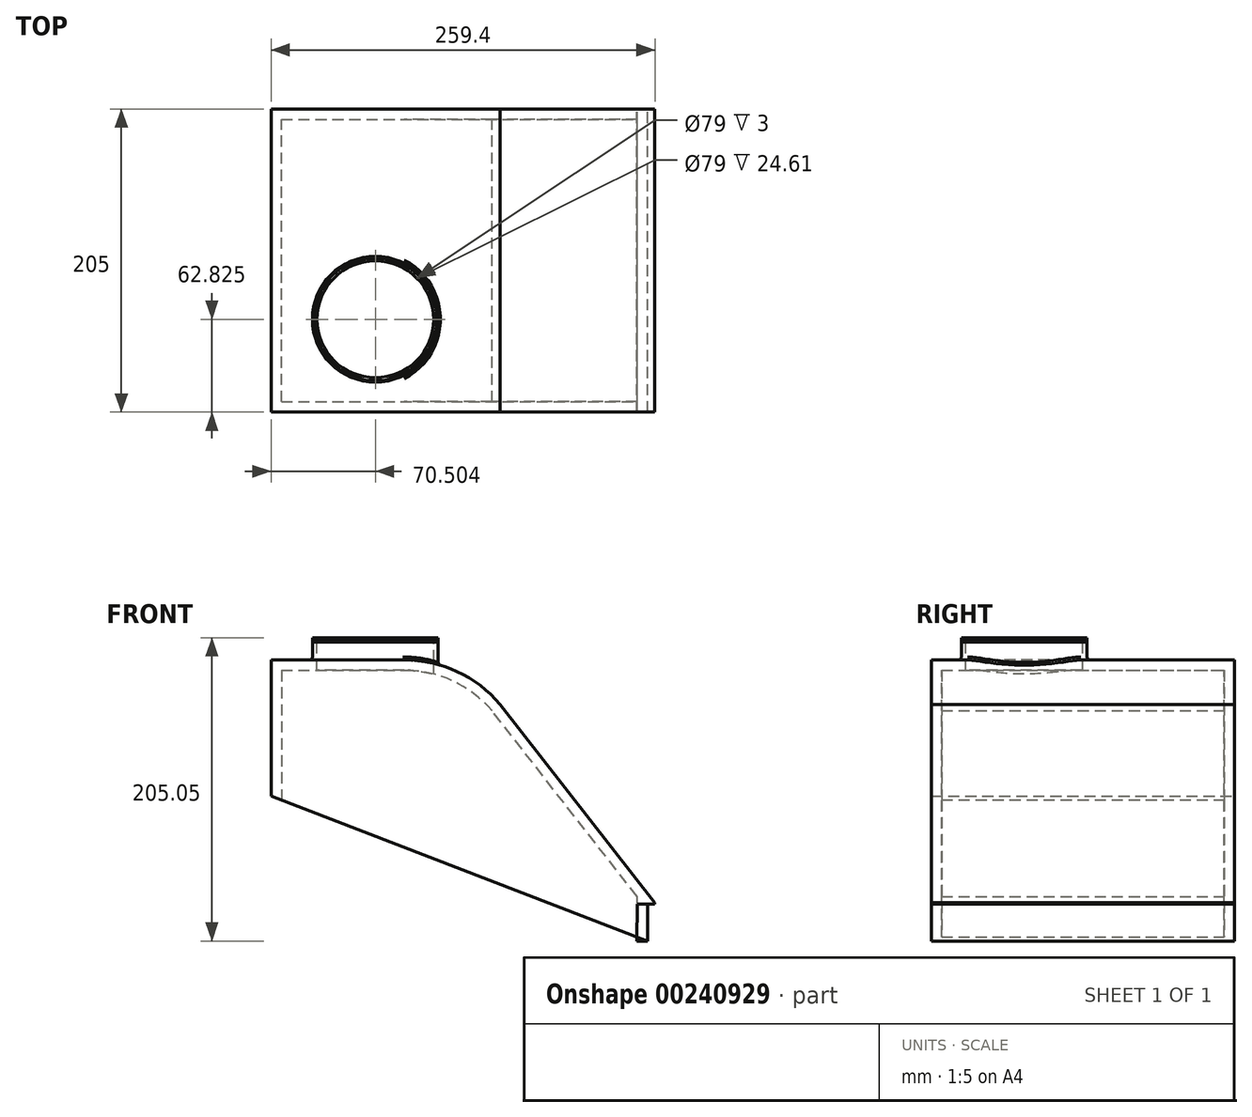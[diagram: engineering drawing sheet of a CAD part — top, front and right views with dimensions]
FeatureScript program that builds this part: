
annotation { "Feature Type Name" : "Feature", "Feature Type Description" : "" }
export const myFeature = defineFeature(function(context is Context, id is Id, definition is map)
    precondition{}
    {
        {
            var Q0;
            Q0=qCreatedBy(makeId("Front.planeOp"),FACE);
            var sketch = newSketch(context, id + "F0", { "sketchPlane" : qUnion([Q0])});
            skLineSegment(sketch, "E0", {"start": v(-34.53, -28) * mm, "end": v(265.47, -28) * mm, "construction": true});
            skLineSegment(sketch, "E1", {"start": v(-17.19, 164) * mm, "end": v(72.81, 164) * mm});
            skLineSegment(sketch, "E2", {"start": v(-17.19, 164) * mm, "end": v(-17.19, 72) * mm});
            skLineSegment(sketch, "E3", {"start": v(-17.19, 72) * mm, "end": v(242.2, -28) * mm});
            skLineSegment(sketch, "E4", {"start": v(242.2, 0) * mm, "end": v(137.6, 134) * mm});
            skLineSegment(sketch, "E5", {"start": v(-17.19, 72) * mm, "end": v(-17.19, -28) * mm, "construction": true});
            skLineSegment(sketch, "E6", {"start": v(242.2, 0) * mm, "end": v(137.2, 0) * mm, "construction": true});
            skArc(sketch, "E7", {"start": v(137.6, 134) * mm, "mid": v(108.5, 156.14) * mm, "end": v(72.81, 164) * mm});
            skLineSegment(sketch, "E8.top", {"start": v(242.2, -1) * mm, "end": v(237.2, -1) * mm});
            skLineSegment(sketch, "E9", {"start": v(242.2, 0) * mm, "end": v(242.2, -1) * mm});
            skLineSegment(sketch, "E10", {"start": v(237.14, -26.05) * mm, "end": v(237.2, -1) * mm});
            skPoint(sketch, "E11", {"position": v(237.14, -26.05) * mm});
            skPoint(sketch, "E12", {"position": v(242.2, -28) * mm});
            skSolve(sketch);
        }
        {
            var Q0;
            Q0=makeQuery(id+"F0.imprint","IMPRINT",FACE,{"disambiguationData":[TD([[makeQuery(id+"F0.imprint","IMPRINT",EDGE,{"derivedFrom":sQuery(id+"F0.wireOp",EDGE,"E1")}),-1.0]])]});
            extrude(context, id + "F1", {"entities" : qUnion([Q0]), "depth" : 100 * mm});
        }
        {
            var Q0;
            Q0=makeQuery(id+"F1.opExtrude","CAP_FACE",FACE,{"disambiguationData":[OSD([sQuery(id+"F0.wireOp",EDGE,"E1"),sQuery(id+"F0.wireOp",EDGE,"E2"),sQuery(id+"F0.wireOp",EDGE,"E3"),sQuery(id+"F0.wireOp",EDGE,"E4"),sQuery(id+"F0.wireOp",EDGE,"E7"),sQuery(id+"F0.wireOp",EDGE,"E8.top"),sQuery(id+"F0.wireOp",EDGE,"E9"),sQuery(id+"F0.wireOp",EDGE,"E10")])],"isStart":false});
            extrude(context, id + "F2", {"entities" : qUnion([Q0]), "operationType" : NewBodyOperationType.ADD, "depth" : 105 * mm});
        }
        {
            var Q0;
            {var subQ0=sQuery(id+"F0.wireOp",EDGE,"E3");Q0=makeQuery(id+"F2.boolean.opBoolean","MERGE",FACE,{"derivedFrom":[makeQuery(id+"F1.opExtrude","SWEPT_FACE",FACE,{"disambiguationData":[OSD([subQ0])]}),makeQuery(id+"F2.opExtrude","SWEPT_FACE",FACE,{"disambiguationData":[OSD([subQ0])]})]});}
            shell(context, id + "F3", {"entities" : qUnion([Q0]), "thickness" : 7 * mm});
        }
        {
            var Q0;
            {var subQ0=sQuery(id+"F0.wireOp",EDGE,"E1");Q0=makeQuery(id+"F2.boolean.opBoolean","MERGE",FACE,{"derivedFrom":[makeQuery(id+"F1.opExtrude","SWEPT_FACE",FACE,{"disambiguationData":[OSD([subQ0])]}),makeQuery(id+"F2.opExtrude","SWEPT_FACE",FACE,{"disambiguationData":[OSD([subQ0])]})]});}
            cPlane(context, id + "F4", {"entities" : qUnion([Q0]), "cplaneType" : CPlaneType.OFFSET, "offset" : 15 * mm, "width" : 150 * mm, "height" : 150 * mm});
        }
        {
            var Q0;
            Q0=qCreatedBy(id+"F4.planeOp",FACE);
            var sketch = newSketch(context, id + "F5", { "sketchPlane" : qUnion([Q0])});
            skCircle(sketch, "E13", {"center": v(53.31, -142.18) * mm, "radius": 42.5 * mm});
            skLineSegment(sketch, "E14", {"start": v(10.81, 14.75) * mm, "end": v(10.81, -239.37) * mm, "construction": true});
            skLineSegment(sketch, "E15", {"start": v(-63, -185) * mm, "end": v(117.93, -185) * mm, "construction": true});
            skSolve(sketch);
        }
        {
            var Q0;
            Q0=makeQuery(id+"F5.imprint","IMPRINT",FACE,{"disambiguationData":[TD([[makeQuery(id+"F5.imprint","IMPRINT",EDGE,{"derivedFrom":sQuery(id+"F5.wireOp",EDGE,"E13")}),1.0]])]});
            extrude(context, id + "F6", {"entities" : qUnion([Q0]), "operationType" : NewBodyOperationType.ADD, "oppositeDirection" : true, "depth" : 20 * mm});
        }
        {
            var Q0;
            Q0=makeQuery(id+"F6.opExtrude","CAP_FACE",FACE,{"disambiguationData":[OSD([sQuery(id+"F5.wireOp",EDGE,"E13")])],"isStart":true});
            extrude(context, id + "F7", {"entities" : qUnion([Q0]), "oppositeDirection" : true, "depth" : 3 * mm});
        }
        {
            var Q0;
            Q0=makeQuery(id+"F6.opExtrude","CAP_FACE",FACE,{"disambiguationData":[OSD([sQuery(id+"F5.wireOp",EDGE,"E13")])],"isStart":true});
            var sketch = newSketch(context, id + "F8", { "sketchPlane" : qUnion([Q0])});
            skCircle(sketch, "E16", {"center": v(53.31, -142.18) * mm, "radius": 39.5 * mm});
            skSolve(sketch);
        }
        {
            var Q0;
            Q0=makeQuery(id+"F8.imprint","IMPRINT",FACE,{"disambiguationData":[TD([[makeQuery(id+"F8.imprint","IMPRINT",EDGE,{"derivedFrom":sQuery(id+"F8.wireOp",EDGE,"E16")}),1.0]])]});
            extrude(context, id + "F9", {"entities" : qUnion([Q0]), "operationType" : NewBodyOperationType.REMOVE, "endBound" : BoundingType.THROUGH_ALL, "oppositeDirection" : true, "depth" : 25 * mm});
        }
        {
            var Q0;
            Q0=makeQuery(id+"F7.opExtrude","CAP_FACE",FACE,{"disambiguationData":[OSD([sQuery(id+"F5.wireOp",EDGE,"E13")])],"isStart":true});
            extrude(context, id + "F10", {"entities" : qUnion([Q0]), "oppositeDirection" : true, "depth" : 4 * mm});
        }
        {
            var Q0;
            Q0=makeQuery(id+"F10.opExtrude","SWEPT_BODY",BODY,{"disambiguationData":[OSD([sQuery(id+"F5.wireOp",EDGE,"E13")])]});
            deleteBodies(context, id + "F11", {"entities" : qUnion([Q0])});
        }
        {
            var Q0;
            Q0=makeQuery(id+"F7.opExtrude","CAP_EDGE",EDGE,{"disambiguationData":[OSD([sQuery(id+"F5.wireOp",EDGE,"E13")])],"isStart":true});
            chamfer(context, id + "F12", {"entities" : qUnion([Q0]), "width" : 1 * mm, "tangentPropagation" : true});
        }
        {
            var Q0;
            {var subQ0=sQuery(id+"F0.wireOp",EDGE,"E1");Q0=makeQuery(id+"F6.boolean.opBoolean","INTERSECT",EDGE,{"derivedFrom":[makeQuery(id+"F2.boolean.opBoolean","MERGE",FACE,{"derivedFrom":[makeQuery(id+"F1.opExtrude","SWEPT_FACE",FACE,{"disambiguationData":[OSD([subQ0])]}),makeQuery(id+"F2.opExtrude","SWEPT_FACE",FACE,{"disambiguationData":[OSD([subQ0])]})]}),makeQuery(id+"F6.opExtrude","SWEPT_FACE",FACE,{"disambiguationData":[OSD([sQuery(id+"F5.wireOp",EDGE,"E13")])]})]});}
            var Q1;
            {var subQ0=sQuery(id+"F0.wireOp",EDGE,"E7");Q1=makeQuery(id+"F6.boolean.opBoolean","INTERSECT",EDGE,{"derivedFrom":[makeQuery(id+"F2.boolean.opBoolean","MERGE",FACE,{"derivedFrom":[makeQuery(id+"F1.opExtrude","SWEPT_FACE",FACE,{"disambiguationData":[OSD([subQ0])]}),makeQuery(id+"F2.opExtrude","SWEPT_FACE",FACE,{"disambiguationData":[OSD([subQ0])]})]}),makeQuery(id+"F6.opExtrude","SWEPT_FACE",FACE,{"disambiguationData":[OSD([sQuery(id+"F5.wireOp",EDGE,"E13")])]})]});}
            fillet(context, id + "F13", {"entities" : qUnion([Q0, Q1]), "radius" : 2 * mm, "tangentPropagation" : true, "allowEdgeOverflow" : false});
        }
        {
            var Q0;
            {var subQ0=sQuery(id+"F0.wireOp",EDGE,"E10");Q0=makeQuery(id+"F2.boolean.opBoolean","MERGE",FACE,{"derivedFrom":[makeQuery(id+"F1.opExtrude","SWEPT_FACE",FACE,{"disambiguationData":[OSD([subQ0])]}),makeQuery(id+"F2.opExtrude","SWEPT_FACE",FACE,{"disambiguationData":[OSD([subQ0])]})]});}
            extrude(context, id + "F14", {"entities" : qUnion([Q0]), "oppositeDirection" : true, "depth" : 7 * mm});
        }
    });
